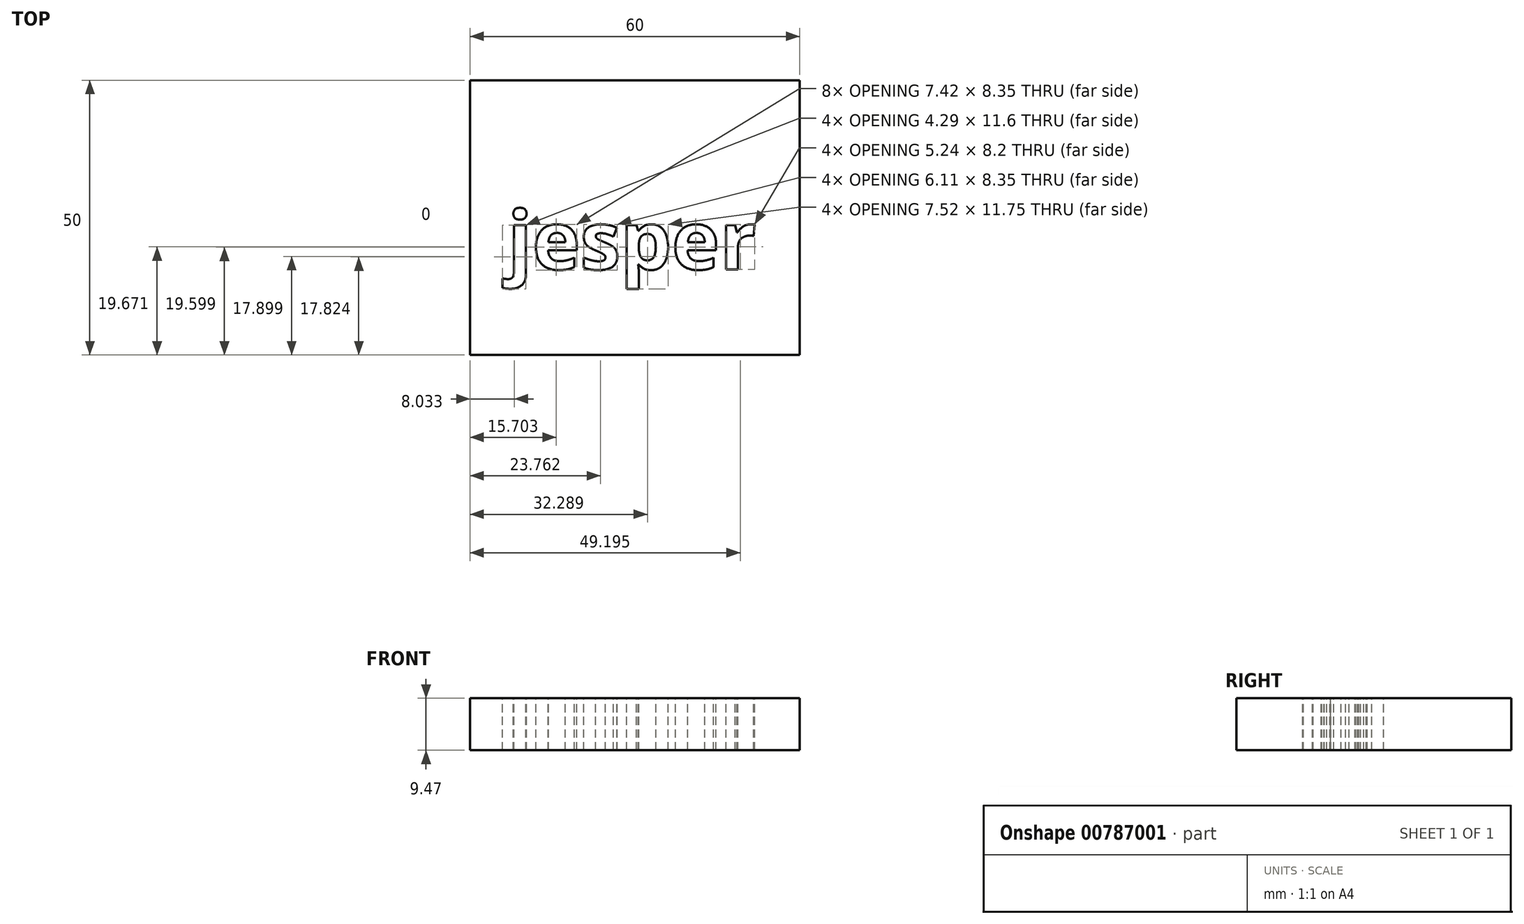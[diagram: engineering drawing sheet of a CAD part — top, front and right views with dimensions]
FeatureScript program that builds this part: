
annotation { "Feature Type Name" : "Feature", "Feature Type Description" : "" }
export const myFeature = defineFeature(function(context is Context, id is Id, definition is map)
    precondition{}
    {
        {
            var Q0;
            Q0=qCreatedBy(makeId("Top.planeOp"),FACE);
            var sketch = newSketch(context, id + "F0", { "sketchPlane" : qUnion([Q0])});
            skLineSegment(sketch, "E0.bottom", {"start": v(20.42, 70.43) * mm, "end": v(80.42, 70.43) * mm});
            skLineSegment(sketch, "E0.top", {"start": v(20.42, 20.43) * mm, "end": v(80.42, 20.43) * mm});
            skLineSegment(sketch, "E0.left", {"start": v(20.42, 70.43) * mm, "end": v(20.42, 20.43) * mm});
            skLineSegment(sketch, "E0.right", {"start": v(80.42, 70.43) * mm, "end": v(80.42, 20.43) * mm});
            skSolve(sketch);
        }
        {
            var Q0;
            Q0=makeQuery(id+"F0.imprint","IMPRINT",FACE,{"disambiguationData":[TD([[makeQuery(id+"F0.imprint","IMPRINT",EDGE,{"derivedFrom":sQuery(id+"F0.wireOp",EDGE,"E0.bottom")}),-1.0]])]});
            extrude(context, id + "F1", {"entities" : qUnion([Q0]), "depth" : 9.47 * mm, "offsetDistance" : 25 * mm});
        }
        {
            var Q0;
            Q0=makeQuery(id+"F1.opExtrude","CAP_FACE",FACE,{"disambiguationData":[OSD([sQuery(id+"F0.wireOp",EDGE,"E0.bottom"),sQuery(id+"F0.wireOp",EDGE,"E0.top"),sQuery(id+"F0.wireOp",EDGE,"E0.left"),sQuery(id+"F0.wireOp",EDGE,"E0.right")])],"isStart":false});
            var sketch = newSketch(context, id + "F2", { "sketchPlane" : qUnion([Q0])});
            skText(sketch, "E1", { "text": "jesper", "fontName": "OpenSans-Bold.ttf"});
            const initialGuessF2  = {"E1": [0.02725, 0.036, 1, 0, 0.01062]};
            skSetInitialGuess(sketch, initialGuessF2);
            skSolve(sketch);
        }
        {
            var Q0;
            Q0=makeQuery(id+"F2.imprint","IMPRINT",FACE,{"disambiguationData":[TD([[makeQuery(id+"F2.imprint","IMPRINT",EDGE,{"derivedFrom":sQuery(id+"F2.wireOp",EDGE,"E1.sketch_text.stroke-35")}),-1.0]])]});
            var Q1;
            Q1=makeQuery(id+"F2.imprint","IMPRINT",FACE,{"disambiguationData":[TD([[makeQuery(id+"F2.imprint","IMPRINT",EDGE,{"derivedFrom":sQuery(id+"F2.wireOp",EDGE,"E1.sketch_text.stroke-61")}),-1.0]])]});
            var Q2;
            Q2=makeQuery(id+"F2.imprint","IMPRINT",FACE,{"disambiguationData":[TD([[makeQuery(id+"F2.imprint","IMPRINT",EDGE,{"derivedFrom":sQuery(id+"F2.wireOp",EDGE,"E1.sketch_text.stroke-84")}),-1.0]])]});
            var Q3;
            Q3=makeQuery(id+"F2.imprint","IMPRINT",FACE,{"disambiguationData":[TD([[makeQuery(id+"F2.imprint","IMPRINT",EDGE,{"derivedFrom":sQuery(id+"F2.wireOp",EDGE,"E1.sketch_text.stroke-15")}),-1.0]])]});
            var Q4;
            Q4=makeQuery(id+"F2.imprint","IMPRINT",FACE,{"disambiguationData":[TD([[makeQuery(id+"F2.imprint","IMPRINT",EDGE,{"derivedFrom":sQuery(id+"F2.wireOp",EDGE,"E1.sketch_text.stroke-0")}),-1.0]])]});
            var Q5;
            Q5=makeQuery(id+"F2.imprint","IMPRINT",FACE,{"disambiguationData":[TD([[makeQuery(id+"F2.imprint","IMPRINT",EDGE,{"derivedFrom":sQuery(id+"F2.wireOp",EDGE,"E1.sketch_text.stroke-10")}),-1.0]])]});
            var Q6;
            Q6=makeQuery(id+"F2.imprint","IMPRINT",FACE,{"disambiguationData":[TD([[makeQuery(id+"F2.imprint","IMPRINT",EDGE,{"derivedFrom":sQuery(id+"F2.wireOp",EDGE,"E1.sketch_text.stroke-104")}),-1.0]])]});
            extrude(context, id + "F3", {"entities" : qUnion([Q0, Q1, Q2, Q3, Q4, Q5, Q6]), "operationType" : NewBodyOperationType.REMOVE, "oppositeDirection" : true, "depth" : 10 * mm, "offsetDistance" : 25 * mm});
        }
    });
